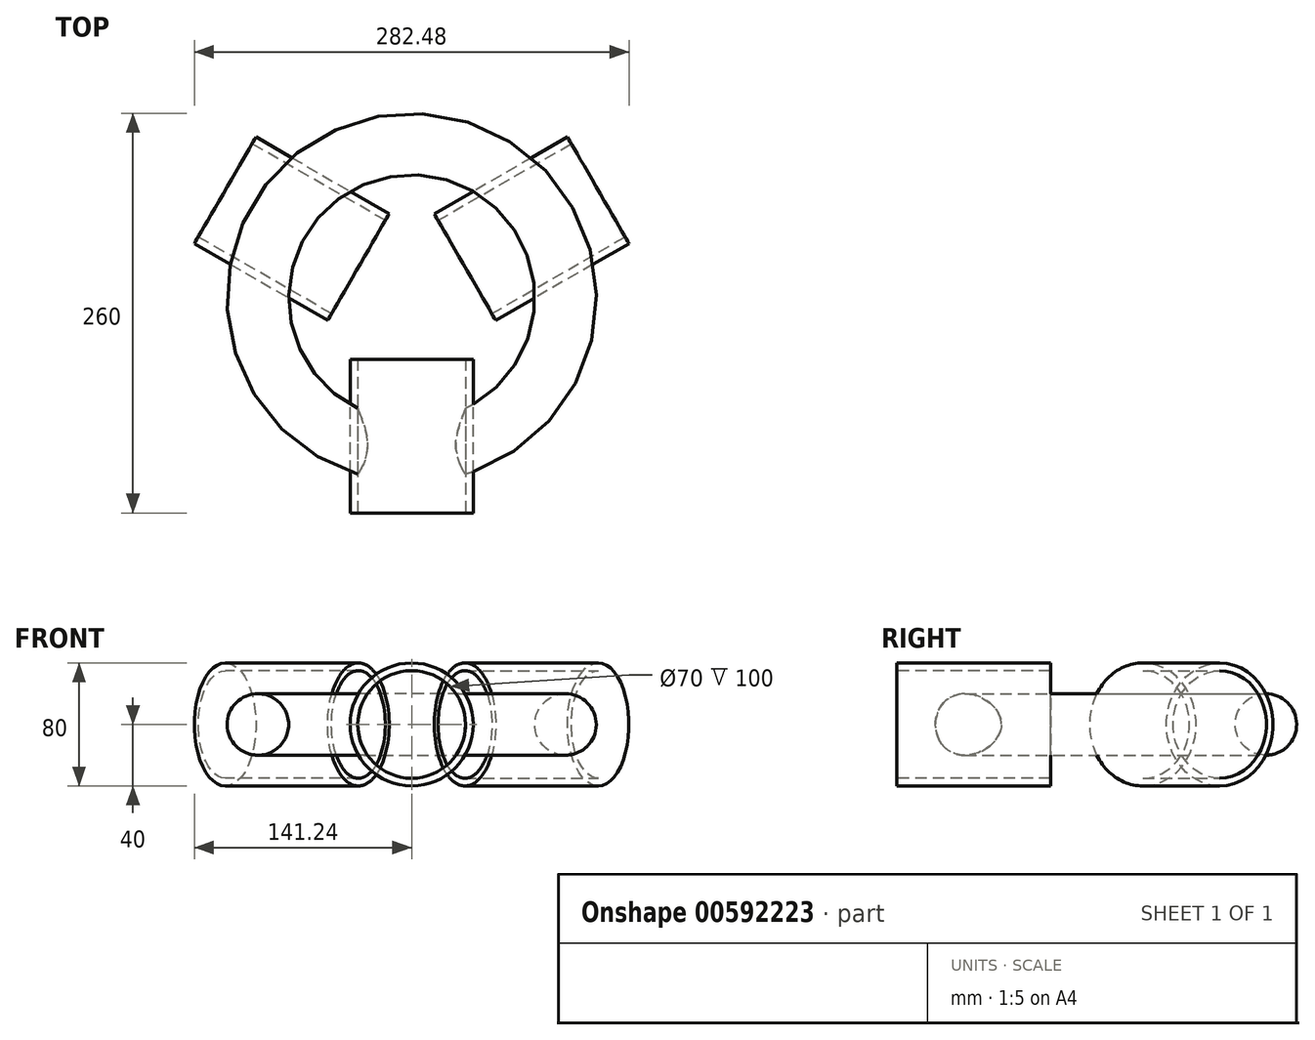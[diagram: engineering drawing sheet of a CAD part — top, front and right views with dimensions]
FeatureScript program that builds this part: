
annotation { "Feature Type Name" : "Feature", "Feature Type Description" : "" }
export const myFeature = defineFeature(function(context is Context, id is Id, definition is map)
    precondition{}
    {
        {
            var Q0;
            Q0=qCreatedBy(makeId("Front.planeOp"),FACE);
            var sketch = newSketch(context, id + "F0", { "sketchPlane" : qUnion([Q0])});
            skCircle(sketch, "E0", {"center": v(100, 0) * mm, "radius": 20 * mm});
            skLineSegment(sketch, "E1", {"start": v(0, 70.09) * mm, "end": v(0, -62.26) * mm, "construction": true});
            skSolve(sketch);
        }
        {
            var Q0;
            Q0 = qSketchRegion(id + "F0", true);
            var Q1;
            Q1=sQuery(id+"F0.wireOp",EDGE,"E1");
            revolve(context, id + "F1", {"entities" : qUnion([Q0]), "axis" : qUnion([Q1]), "revolveType" : RevolveType.FULL});
        }
        {
            var Q0;
            Q0=qCreatedBy(makeId("Front.planeOp"),FACE);
            cPlane(context, id + "F2", {"entities" : qUnion([Q0]), "cplaneType" : CPlaneType.OFFSET, "offset" : 40 * mm, "width" : 150 * mm, "height" : 150 * mm});
        }
        {
            var Q0;
            Q0=qCreatedBy(id+"F2.planeOp",FACE);
            var sketch = newSketch(context, id + "F3", { "sketchPlane" : qUnion([Q0])});
            skCircle(sketch, "E2", {"center": v(0, 0) * mm, "radius": 40 * mm});
            skSolve(sketch);
        }
        {
            var Q0;
            Q0 = qSketchRegion(id + "F3", true);
            extrude(context, id + "F4", {"entities" : qUnion([Q0]), "depth" : 100 * mm, "offsetDistance" : 25 * mm});
        }
        {
            var Q0;
            Q0=makeQuery(id+"F4.opExtrude","CAP_FACE",FACE,{"disambiguationData":[OSD([sQuery(id+"F3.wireOp",EDGE,"E2")])],"isStart":false});
            var sketch = newSketch(context, id + "F5", { "sketchPlane" : qUnion([Q0])});
            skCircle(sketch, "E3", {"center": v(0, 0) * mm, "radius": 35 * mm});
            skSolve(sketch);
        }
        {
            var Q0;
            Q0 = qSketchRegion(id + "F5", true);
            extrude(context, id + "F6", {"entities" : qUnion([Q0]), "operationType" : NewBodyOperationType.REMOVE, "oppositeDirection" : true, "depth" : 100 * mm, "offsetDistance" : 25 * mm});
        }
        {
            var Q0;
            Q0=makeQuery(id+"F4.opExtrude","SWEPT_BODY",BODY,{"disambiguationData":[OSD([sQuery(id+"F3.wireOp",EDGE,"E2")])]});
            var Q1;
            Q1=sQuery(id+"F0.wireOp",EDGE,"E1");
            circularPattern(context, id + "F7", {"entities" : qUnion([Q0]), "axis" : qUnion([Q1]), "angle" : 360 * degree, "instanceCount" : 3, "equalSpace" : true});
        }
    });
